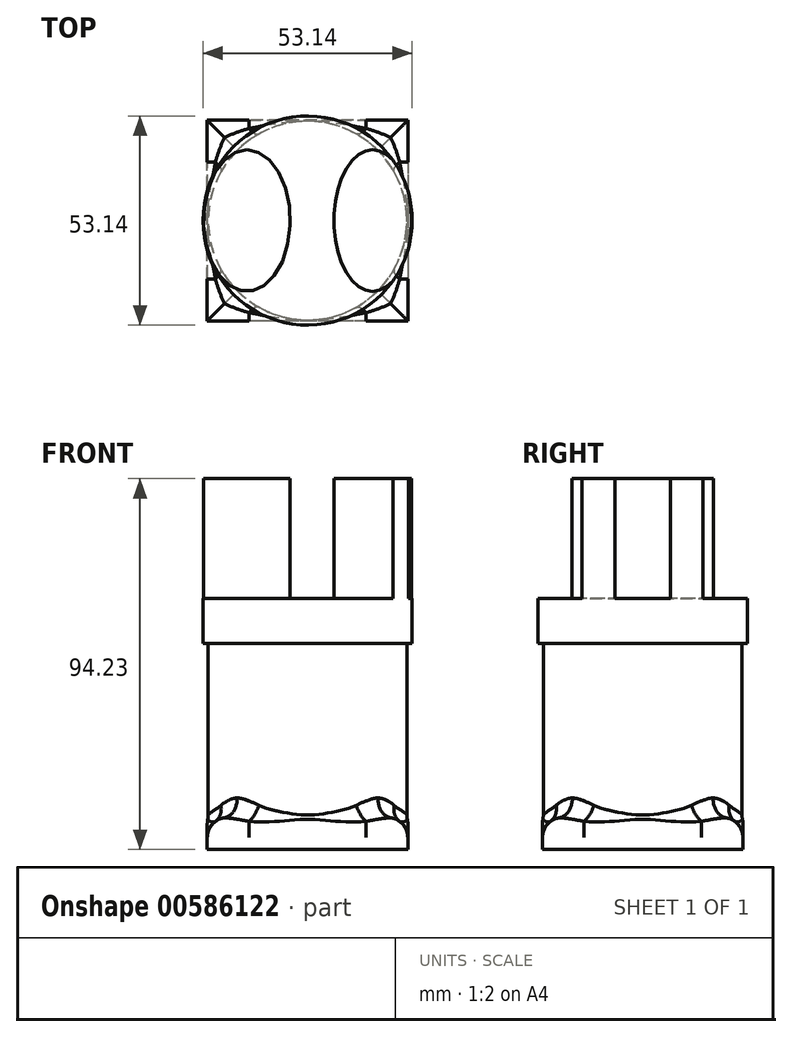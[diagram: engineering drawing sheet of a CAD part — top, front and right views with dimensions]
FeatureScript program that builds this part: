
annotation { "Feature Type Name" : "Feature", "Feature Type Description" : "" }
export const myFeature = defineFeature(function(context is Context, id is Id, definition is map)
    precondition{}
    {
        {
            var Q0;
            Q0=qCreatedBy(makeId("Top.planeOp"),FACE);
            var sketch = newSketch(context, id + "F0", { "sketchPlane" : qUnion([Q0])});
            skLineSegment(sketch, "E0.bottom", {"start": v(25.47, 25.47) * mm, "end": v(-25.47, 25.47) * mm});
            skLineSegment(sketch, "E0.top", {"start": v(25.47, -25.47) * mm, "end": v(-25.47, -25.47) * mm});
            skLineSegment(sketch, "E0.left", {"start": v(25.47, 25.47) * mm, "end": v(25.47, -25.47) * mm});
            skLineSegment(sketch, "E0.right", {"start": v(-25.47, 25.47) * mm, "end": v(-25.47, -25.47) * mm});
            skPoint(sketch, "E0.middle", {"position": v(0, 0) * mm});
            skSolve(sketch);
        }
        {
            var Q0;
            Q0=makeQuery(id+"F0.imprint","IMPRINT",FACE,{"disambiguationData":[TD([[makeQuery(id+"F0.imprint","IMPRINT",EDGE,{"derivedFrom":sQuery(id+"F0.wireOp",EDGE,"E0.bottom")}),1.0]])]});
            extrude(context, id + "F1", {"entities" : qUnion([Q0]), "depth" : 8.13 * mm, "offsetDistance" : 25.4 * mm});
        }
        {
            var Q0;
            Q0=makeQuery(id+"F1.opExtrude","CAP_FACE",FACE,{"disambiguationData":[OSD([sQuery(id+"F0.wireOp",EDGE,"E0.bottom"),sQuery(id+"F0.wireOp",EDGE,"E0.top"),sQuery(id+"F0.wireOp",EDGE,"E0.left"),sQuery(id+"F0.wireOp",EDGE,"E0.right")])],"isStart":false});
            var sketch = newSketch(context, id + "F2", { "sketchPlane" : qUnion([Q0])});
            skCircle(sketch, "E1", {"center": v(0, 0) * mm, "radius": 25.24 * mm});
            skSolve(sketch);
        }
        {
            var Q0;
            Q0=makeQuery(id+"F2.imprint","IMPRINT",FACE,{"disambiguationData":[TD([[makeQuery(id+"F2.imprint","IMPRINT",EDGE,{"derivedFrom":sQuery(id+"F2.wireOp",EDGE,"E1")}),1.0]])]});
            extrude(context, id + "F3", {"entities" : qUnion([Q0]), "operationType" : NewBodyOperationType.ADD, "depth" : 44.2 * mm, "offsetDistance" : 25.4 * mm});
        }
        {
            var Q0;
            Q0=makeQuery(id+"F1.opExtrude","CAP_EDGE",EDGE,{"disambiguationData":[OSD([sQuery(id+"F0.wireOp",EDGE,"E0.top")])],"isStart":false});
            var Q1;
            Q1=makeQuery(id+"F1.opExtrude","CAP_EDGE",EDGE,{"disambiguationData":[OSD([sQuery(id+"F0.wireOp",EDGE,"E0.right")])],"isStart":false});
            var Q2;
            Q2=makeQuery(id+"F1.opExtrude","CAP_EDGE",EDGE,{"disambiguationData":[OSD([sQuery(id+"F0.wireOp",EDGE,"E0.bottom")])],"isStart":false});
            var Q3;
            Q3=makeQuery(id+"F1.opExtrude","CAP_EDGE",EDGE,{"disambiguationData":[OSD([sQuery(id+"F0.wireOp",EDGE,"E0.left")])],"isStart":false});
            fillet(context, id + "F4", {"entities" : qUnion([Q0, Q1, Q2, Q3]), "radius" : 5.08 * mm, "tangentPropagation" : true, "allowEdgeOverflow" : false});
        }
        {
            var Q0;
            Q0=makeQuery(id+"F4.opFillet","BLEND_EDGE",EDGE,{"blendedFrom":[makeQuery(id+"F1.opExtrude","CAP_EDGE",EDGE,{"disambiguationData":[OSD([sQuery(id+"F0.wireOp",EDGE,"E0.right")])],"isStart":false}),makeQuery(id+"F3.opExtrude","SWEPT_FACE",FACE,{"disambiguationData":[OSD([sQuery(id+"F2.wireOp",EDGE,"E1")])]})],"blendedInto":[makeQuery(id+"F3.opExtrude","SWEPT_FACE",FACE,{"disambiguationData":[OSD([sQuery(id+"F2.wireOp",EDGE,"E1")])]})]});
            var Q1;
            Q1=makeQuery(id+"F4.opFillet","BLEND_EDGE",EDGE,{"blendedFrom":[makeQuery(id+"F1.opExtrude","CAP_EDGE",EDGE,{"disambiguationData":[OSD([sQuery(id+"F0.wireOp",EDGE,"E0.top")])],"isStart":false}),makeQuery(id+"F3.opExtrude","SWEPT_FACE",FACE,{"disambiguationData":[OSD([sQuery(id+"F2.wireOp",EDGE,"E1")])]})],"blendedInto":[makeQuery(id+"F3.opExtrude","SWEPT_FACE",FACE,{"disambiguationData":[OSD([sQuery(id+"F2.wireOp",EDGE,"E1")])]})]});
            var Q2;
            Q2=makeQuery(id+"F3.opExtrude","CAP_EDGE",EDGE,{"disambiguationData":[OSD([sQuery(id+"F2.wireOp",EDGE,"E1")])],"isStart":true});
            var Q3;
            Q3=makeQuery(id+"F4.opFillet","BLEND_EDGE",EDGE,{"blendedFrom":[makeQuery(id+"F1.opExtrude","CAP_EDGE",EDGE,{"disambiguationData":[OSD([sQuery(id+"F0.wireOp",EDGE,"E0.left")])],"isStart":false}),makeQuery(id+"F3.opExtrude","SWEPT_FACE",FACE,{"disambiguationData":[OSD([sQuery(id+"F2.wireOp",EDGE,"E1")])]})],"blendedInto":[makeQuery(id+"F3.opExtrude","SWEPT_FACE",FACE,{"disambiguationData":[OSD([sQuery(id+"F2.wireOp",EDGE,"E1")])]})]});
            var Q4;
            Q4=makeQuery(id+"F4.opFillet","BLEND_EDGE",EDGE,{"blendedFrom":[makeQuery(id+"F1.opExtrude","CAP_EDGE",EDGE,{"disambiguationData":[OSD([sQuery(id+"F0.wireOp",EDGE,"E0.bottom")])],"isStart":false}),makeQuery(id+"F3.opExtrude","SWEPT_FACE",FACE,{"disambiguationData":[OSD([sQuery(id+"F2.wireOp",EDGE,"E1")])]})],"blendedInto":[makeQuery(id+"F3.opExtrude","SWEPT_FACE",FACE,{"disambiguationData":[OSD([sQuery(id+"F2.wireOp",EDGE,"E1")])]})]});
            fillet(context, id + "F5", {"entities" : qUnion([Q0, Q1, Q2, Q3, Q4]), "radius" : 5.08 * mm, "tangentPropagation" : true, "allowEdgeOverflow" : false});
        }
        {
            var Q0;
            Q0=makeQuery(id+"F3.opExtrude","CAP_FACE",FACE,{"disambiguationData":[OSD([sQuery(id+"F2.wireOp",EDGE,"E1")])],"isStart":false});
            var sketch = newSketch(context, id + "F6", { "sketchPlane" : qUnion([Q0])});
            skCircle(sketch, "E2", {"center": v(0, 0) * mm, "radius": 26.57 * mm});
            skSolve(sketch);
        }
        {
            var Q0;
            Q0=makeQuery(id+"F6.imprint","IMPRINT",FACE,{"disambiguationData":[TD([[makeQuery(id+"F6.imprint","IMPRINT",EDGE,{"derivedFrom":sQuery(id+"F6.wireOp",EDGE,"E2")}),1.0]])]});
            var Q1;
            Q1=makeQuery(id+"F6.imprint","IMPRINT",FACE,{"disambiguationData":[TD([[makeQuery(id+"F6.imprint","IMPRINT",EDGE,{"derivedFrom":makeQuery(id+"F3.opExtrude","CAP_EDGE",EDGE,{"disambiguationData":[OSD([sQuery(id+"F2.wireOp",EDGE,"E1")])],"isStart":false})}),1.0]])]});
            extrude(context, id + "F7", {"entities" : qUnion([Q0, Q1]), "operationType" : NewBodyOperationType.ADD, "depth" : 11.43 * mm, "offsetDistance" : 25.4 * mm});
        }
        {
            var Q0;
            Q0=makeQuery(id+"F7.opExtrude","CAP_FACE",FACE,{"disambiguationData":[OSD([sQuery(id+"F6.wireOp",EDGE,"E2")])],"isStart":false});
            var sketch = newSketch(context, id + "F8", { "sketchPlane" : qUnion([Q0])});
            skSolve(sketch);
        }
        {
            var Q0;
            Q0=makeQuery(id+"F8.imprint","IMPRINT",FACE,{"disambiguationData":[TD([[makeQuery(id+"F8.imprint","IMPRINT",EDGE,{"derivedFrom":makeQuery(id+"F7.opExtrude","CAP_EDGE",EDGE,{"disambiguationData":[OSD([sQuery(id+"F6.wireOp",EDGE,"E2")])],"isStart":false})}),1.0]])]});
            var sketch = newSketch(context, id + "F9", { "sketchPlane" : qUnion([Q0])});
            skEllipse(sketch, "E3", {"center": v(16.55, 0) * mm, "majorRadius": 17.99 * mm, "minorRadius": 9.86 * mm, "majorAxis": v(0, 1)});
            skEllipse(sketch, "E4", {"center": v(-15.4, 0) * mm, "majorRadius": 17.99 * mm, "minorRadius": 11 * mm, "majorAxis": v(0, 1)});
            skSolve(sketch);
        }
        {
            var Q0;
            {var subQ0=sQuery(id+"F9.wireOp",EDGE,"E3");var subQ1=makeQuery(id+"F8.imprint","IMPRINT",EDGE,{"derivedFrom":makeQuery(id+"F7.opExtrude","CAP_EDGE",EDGE,{"disambiguationData":[OSD([sQuery(id+"F6.wireOp",EDGE,"E2")])],"isStart":false})});var subQ2=makeQuery(id+"F9.imprint","INTERSECT",VERTEX,{"disambiguationData":[OD(0.0)],"derivedFrom":[subQ1,subQ0]});Q0=makeQuery(id+"F9.imprint","IMPRINT",FACE,{"disambiguationData":[TD([[makeQuery(id+"F9.imprint","IMPRINT",EDGE,{"disambiguationData":[TD([[subQ2,-1.0]])],"derivedFrom":subQ0}),1.0]])]});}
            var Q1;
            Q1=makeQuery(id+"F9.imprint","IMPRINT",FACE,{"disambiguationData":[TD([[makeQuery(id+"F9.imprint","IMPRINT",EDGE,{"derivedFrom":sQuery(id+"F9.wireOp",EDGE,"E4")}),1.0]])]});
            extrude(context, id + "F10", {"entities" : qUnion([Q0, Q1]), "operationType" : NewBodyOperationType.ADD, "depth" : 30.48 * mm, "offsetDistance" : 25.4 * mm});
        }
    });
